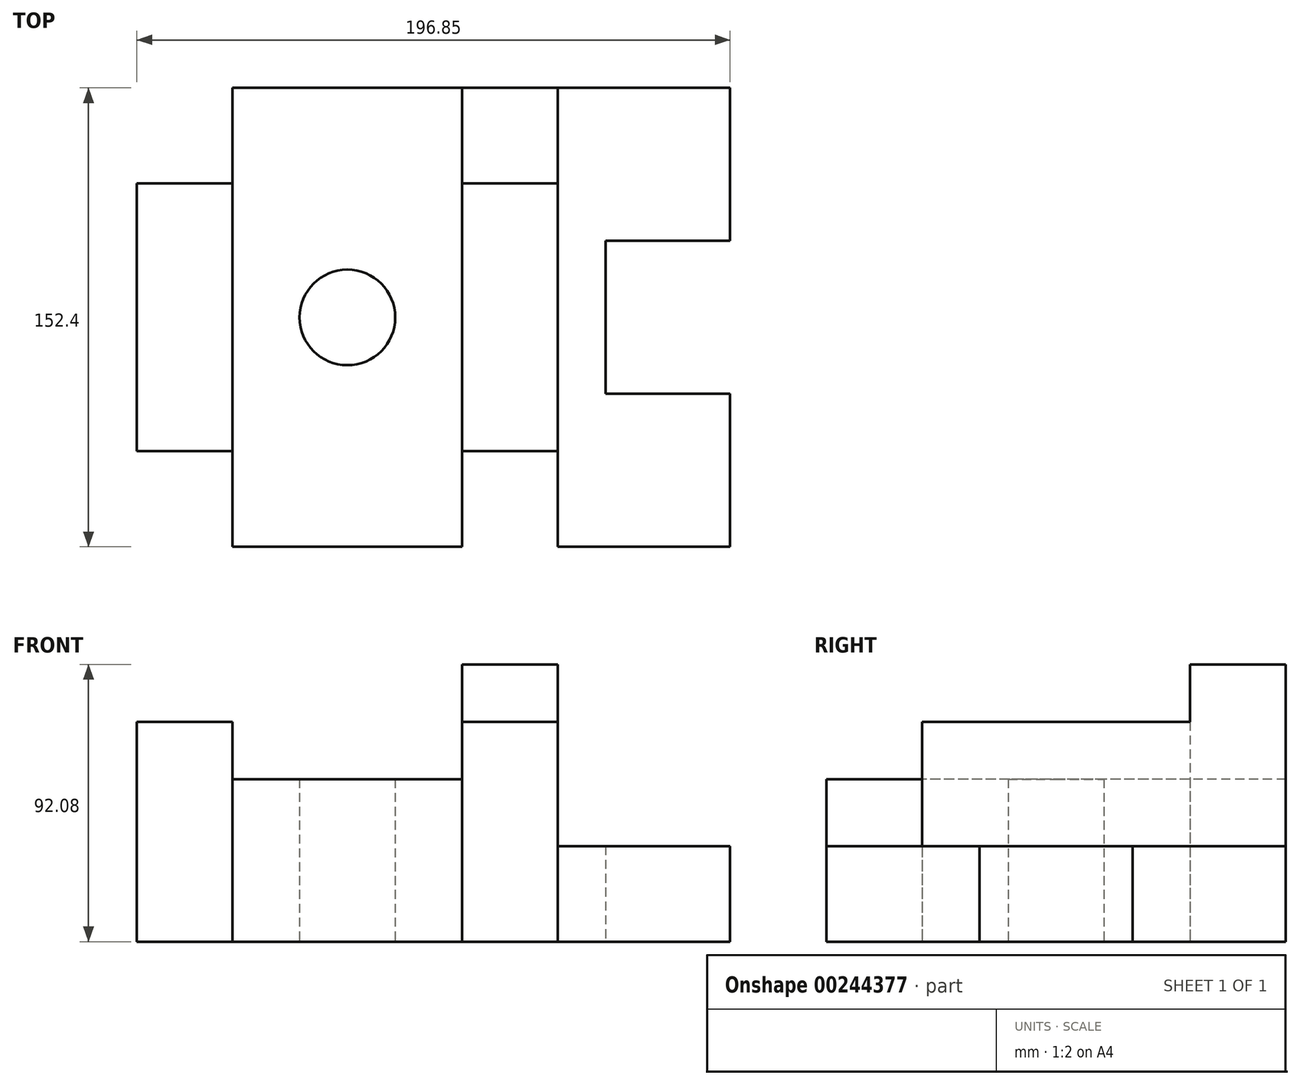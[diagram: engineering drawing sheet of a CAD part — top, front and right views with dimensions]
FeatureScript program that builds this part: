
annotation { "Feature Type Name" : "Feature", "Feature Type Description" : "" }
export const myFeature = defineFeature(function(context is Context, id is Id, definition is map)
    precondition{}
    {
        {
            var Q0;
            Q0=qCreatedBy(makeId("Top.planeOp"),FACE);
            var sketch = newSketch(context, id + "F0", { "sketchPlane" : qUnion([Q0])});
            skCircle(sketch, "E0", {"center": v(0, 0) * mm, "radius": 15.88 * mm});
            skLineSegment(sketch, "E1.bottom", {"start": v(127, 76.2) * mm, "end": v(-127, 76.2) * mm});
            skLineSegment(sketch, "E1.top", {"start": v(127, -76.2) * mm, "end": v(-127, -76.2) * mm});
            skLineSegment(sketch, "E1.left", {"start": v(127, 76.2) * mm, "end": v(127, 25.4) * mm});
            skLineSegment(sketch, "E1.right", {"start": v(-127, 76.2) * mm, "end": v(-127, 25.4) * mm});
            skLineSegment(sketch, "E2.top", {"start": v(-127, -25.4) * mm, "end": v(-85.73, -25.4) * mm});
            skLineSegment(sketch, "E2.left", {"start": v(-127, -76.2) * mm, "end": v(-127, -25.4) * mm});
            skLineSegment(sketch, "E3.top", {"start": v(-127, 25.4) * mm, "end": v(-85.73, 25.4) * mm});
            skLineSegment(sketch, "E4.right", {"start": v(-85.73, 25.4) * mm, "end": v(-85.73, -25.4) * mm});
            skLineSegment(sketch, "E5", {"start": v(85.72, 25.4) * mm, "end": v(127, 25.4) * mm});
            skLineSegment(sketch, "E6", {"start": v(85.73, -25.4) * mm, "end": v(127, -25.4) * mm});
            skLineSegment(sketch, "E7.bottom", {"start": v(127, 25.4) * mm, "end": v(85.72, 25.4) * mm});
            skLineSegment(sketch, "E7.top", {"start": v(127, -25.4) * mm, "end": v(85.73, -25.4) * mm});
            skLineSegment(sketch, "E7.right", {"start": v(85.72, 25.4) * mm, "end": v(85.73, -25.4) * mm});
            skLineSegment(sketch, "E8", {"start": v(-127, -76.2) * mm, "end": v(-69.85, -76.2) * mm});
            skLineSegment(sketch, "E9", {"start": v(-69.85, 76.2) * mm, "end": v(-38.1, 76.2) * mm});
            skLineSegment(sketch, "E10.top", {"start": v(-69.85, 44.45) * mm, "end": v(-38.1, 44.45) * mm});
            skLineSegment(sketch, "E10.left", {"start": v(-69.85, 76.2) * mm, "end": v(-69.85, 44.45) * mm});
            skLineSegment(sketch, "E10.right", {"start": v(-38.1, 76.2) * mm, "end": v(-38.1, 44.45) * mm});
            skLineSegment(sketch, "E11.bottom", {"start": v(-69.85, -76.2) * mm, "end": v(-38.1, -76.2) * mm});
            skLineSegment(sketch, "E11.top", {"start": v(-69.85, -44.45) * mm, "end": v(-38.1, -44.45) * mm});
            skLineSegment(sketch, "E11.left", {"start": v(-69.85, -76.2) * mm, "end": v(-69.85, -44.45) * mm});
            skLineSegment(sketch, "E11.right", {"start": v(-38.1, -76.2) * mm, "end": v(-38.1, -44.45) * mm});
            skLineSegment(sketch, "E12", {"start": v(38.1, 76.2) * mm, "end": v(69.85, 76.2) * mm});
            skLineSegment(sketch, "E13.top", {"start": v(38.1, 44.45) * mm, "end": v(69.85, 44.45) * mm});
            skLineSegment(sketch, "E14.bottom", {"start": v(38.1, -76.2) * mm, "end": v(69.85, -76.2) * mm});
            skLineSegment(sketch, "E14.top", {"start": v(38.1, -44.45) * mm, "end": v(69.85, -44.45) * mm});
            skLineSegment(sketch, "E15.trimOffspring", {"start": v(127, -25.4) * mm, "end": v(127, -76.2) * mm});
            skLineSegment(sketch, "E16.trimOffspring", {"start": v(-127, -25.4) * mm, "end": v(-127, -76.2) * mm});
            skLineSegment(sketch, "E17", {"start": v(38.1, 76.2) * mm, "end": v(38.1, -76.2) * mm});
            skLineSegment(sketch, "E18", {"start": v(69.85, 76.2) * mm, "end": v(69.85, -76.2) * mm});
            skLineSegment(sketch, "E19", {"start": v(-69.85, -44.45) * mm, "end": v(-69.85, 44.45) * mm});
            skLineSegment(sketch, "E20", {"start": v(-38.1, 44.45) * mm, "end": v(-38.1, -44.45) * mm});
            skSolve(sketch);
        }
        {
            var Q0;
            Q0=makeQuery(id+"F0.imprint","IMPRINT",FACE,{"disambiguationData":[TD([[makeQuery(id+"F0.imprint","IMPRINT",EDGE,{"derivedFrom":sQuery(id+"F0.wireOp",EDGE,"E9")}),-1.0]])]});
            var Q1;
            Q1=makeQuery(id+"F0.imprint","IMPRINT",FACE,{"disambiguationData":[TD([[makeQuery(id+"F0.imprint","IMPRINT",EDGE,{"derivedFrom":sQuery(id+"F0.wireOp",EDGE,"E13.top")}),1.0]])]});
            var Q2;
            Q2=makeQuery(id+"F0.imprint","IMPRINT",FACE,{"disambiguationData":[TD([[makeQuery(id+"F0.imprint","IMPRINT",EDGE,{"derivedFrom":sQuery(id+"F0.wireOp",EDGE,"E14.bottom")}),1.0]])]});
            var Q3;
            Q3=makeQuery(id+"F0.imprint","IMPRINT",FACE,{"disambiguationData":[TD([[makeQuery(id+"F0.imprint","IMPRINT",EDGE,{"derivedFrom":sQuery(id+"F0.wireOp",EDGE,"E11.bottom")}),1.0]])]});
            extrude(context, id + "F1", {"entities" : qUnion([Q0, Q1, Q2, Q3]), "depth" : 92.07 * mm});
        }
        {
            var Q0;
            {var subQ4=sQuery(id+"F0.wireOp",EDGE,"E3.bottom");Q0=makeQuery(id+"F0.imprint","IMPRINT",FACE,{"disambiguationData":[TD([[makeQuery(id+"F0.imprint","IMPRINT",EDGE,{"derivedFrom":subQ4}),-1.0]])]});}
            var Q1;
            {var subQ1=sQuery(id+"F0.wireOp",EDGE,"E1.left");Q1=makeQuery(id+"F0.imprint","IMPRINT",FACE,{"disambiguationData":[TD([[makeQuery(id+"F0.imprint","IMPRINT",EDGE,{"derivedFrom":subQ1}),-1.0]])]});}
            extrude(context, id + "F2", {"entities" : qUnion([Q0, Q1]), "operationType" : NewBodyOperationType.ADD, "depth" : 31.75 * mm});
        }
        {
            var Q0;
            Q0=makeQuery(id+"F0.imprint","IMPRINT",FACE,{"disambiguationData":[TD([[makeQuery(id+"F0.imprint","IMPRINT",EDGE,{"derivedFrom":sQuery(id+"F0.wireOp",EDGE,"E0")}),-1.0]])]});
            extrude(context, id + "F3", {"entities" : qUnion([Q0]), "operationType" : NewBodyOperationType.ADD, "depth" : 53.97 * mm});
        }
        {
            var Q0;
            Q0=makeQuery(id+"F0.imprint","IMPRINT",FACE,{"disambiguationData":[TD([[makeQuery(id+"F0.imprint","IMPRINT",EDGE,{"derivedFrom":sQuery(id+"F0.wireOp",EDGE,"E10.top")}),-1.0]])]});
            var Q1;
            {var subQ0=sQuery(id+"F0.wireOp",EDGE,"E13.top");Q1=makeQuery(id+"F0.imprint","IMPRINT",FACE,{"disambiguationData":[TD([[makeQuery(id+"F0.imprint","IMPRINT",EDGE,{"derivedFrom":subQ0}),-1.0]])]});}
            extrude(context, id + "F4", {"entities" : qUnion([Q0, Q1]), "operationType" : NewBodyOperationType.ADD, "depth" : 73.02 * mm});
        }
    });
